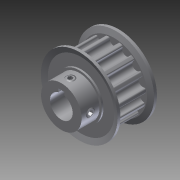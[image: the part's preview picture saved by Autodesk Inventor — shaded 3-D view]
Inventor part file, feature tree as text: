
AUTODESK INVENTOR PART (.ipt)
format: ipt  version: 2012 (Build 160160000, 160)  size: 315,392 bytes
history: native  units: in
note: dims shown in document units (in); Inventor stores cm internally (conversion verified against a paired STEP export)
features: extrude x1, imported_body x1, sketch x1
ambient origin geometry x8: Origin, YZ Plane, XZ Plane, XY Plane, X Axis, Y Axis, Z Axis, Center Point
feature tree (3):
  extrude  "Extrusion1"  Depth=0.0394in
  imported_body  "Base1"
  sketch  "Sketch1"  dims[d0=0.315in d1=0.0394in d4=0.0394in d5=0.1181in d6=0.0787in d7=0.0787in d8=0.3937in d9=0.0in]
